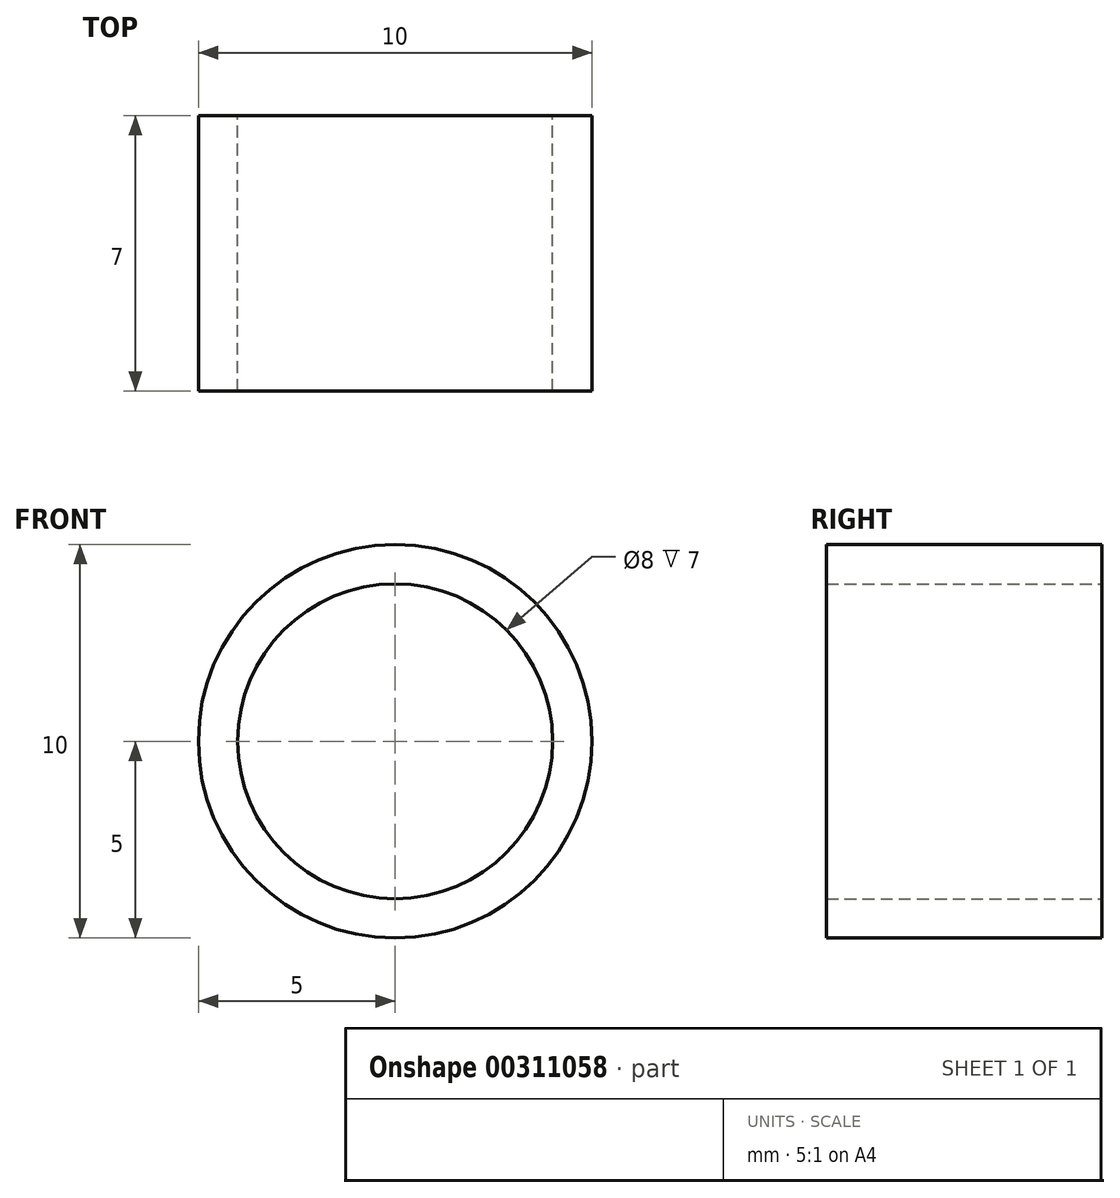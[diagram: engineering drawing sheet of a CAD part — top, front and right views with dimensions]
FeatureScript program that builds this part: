
annotation { "Feature Type Name" : "Feature", "Feature Type Description" : "" }
export const myFeature = defineFeature(function(context is Context, id is Id, definition is map)
    precondition{}
    {
        {
            var Q0;
            Q0=qCreatedBy(makeId("Front.planeOp"),FACE);
            var sketch = newSketch(context, id + "F0", { "sketchPlane" : qUnion([Q0])});
            skCircle(sketch, "E0", {"center": v(0, 0) * mm, "radius": 4 * mm});
            skCircle(sketch, "E1", {"center": v(0, 0) * mm, "radius": 5 * mm});
            skSolve(sketch);
        }
        {
            var Q0;
            Q0=makeQuery(id+"F0.imprint","IMPRINT",FACE,{"disambiguationData":[TD([[makeQuery(id+"F0.imprint","IMPRINT",EDGE,{"derivedFrom":sQuery(id+"F0.wireOp",EDGE,"E0")}),-1.0]])]});
            extrude(context, id + "F1", {"entities" : qUnion([Q0]), "depth" : 7 * mm});
        }
    });
